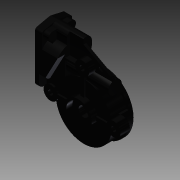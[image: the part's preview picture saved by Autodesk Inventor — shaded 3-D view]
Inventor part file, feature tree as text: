
AUTODESK INVENTOR PART (.ipt)
format: ipt  version: 2016 SP1 (Build 200210100, 210)  size: 293,376 bytes
history: native  units: in
note: dims shown in document units (in); Inventor stores cm internally (conversion verified against a paired STEP export)
features: fillet x1, other x1, imported_body x1
ambient origin geometry x8: Origin, YZ Plane, XZ Plane, XY Plane, X Axis, Y Axis, Z Axis, Center Point
bodies: Body1 (feature_tree)
feature tree (3):
  fillet  "Fillet1"  [1 undecoded]
  other  "AM-2235 gearbox housing.ipt1"
  imported_body  "Base1"
note: 1 required parameter value undecoded (feature->parameter linkage not recoverable at this tier; creation-order binding heuristic only, values carry confidence <= 0.55)
